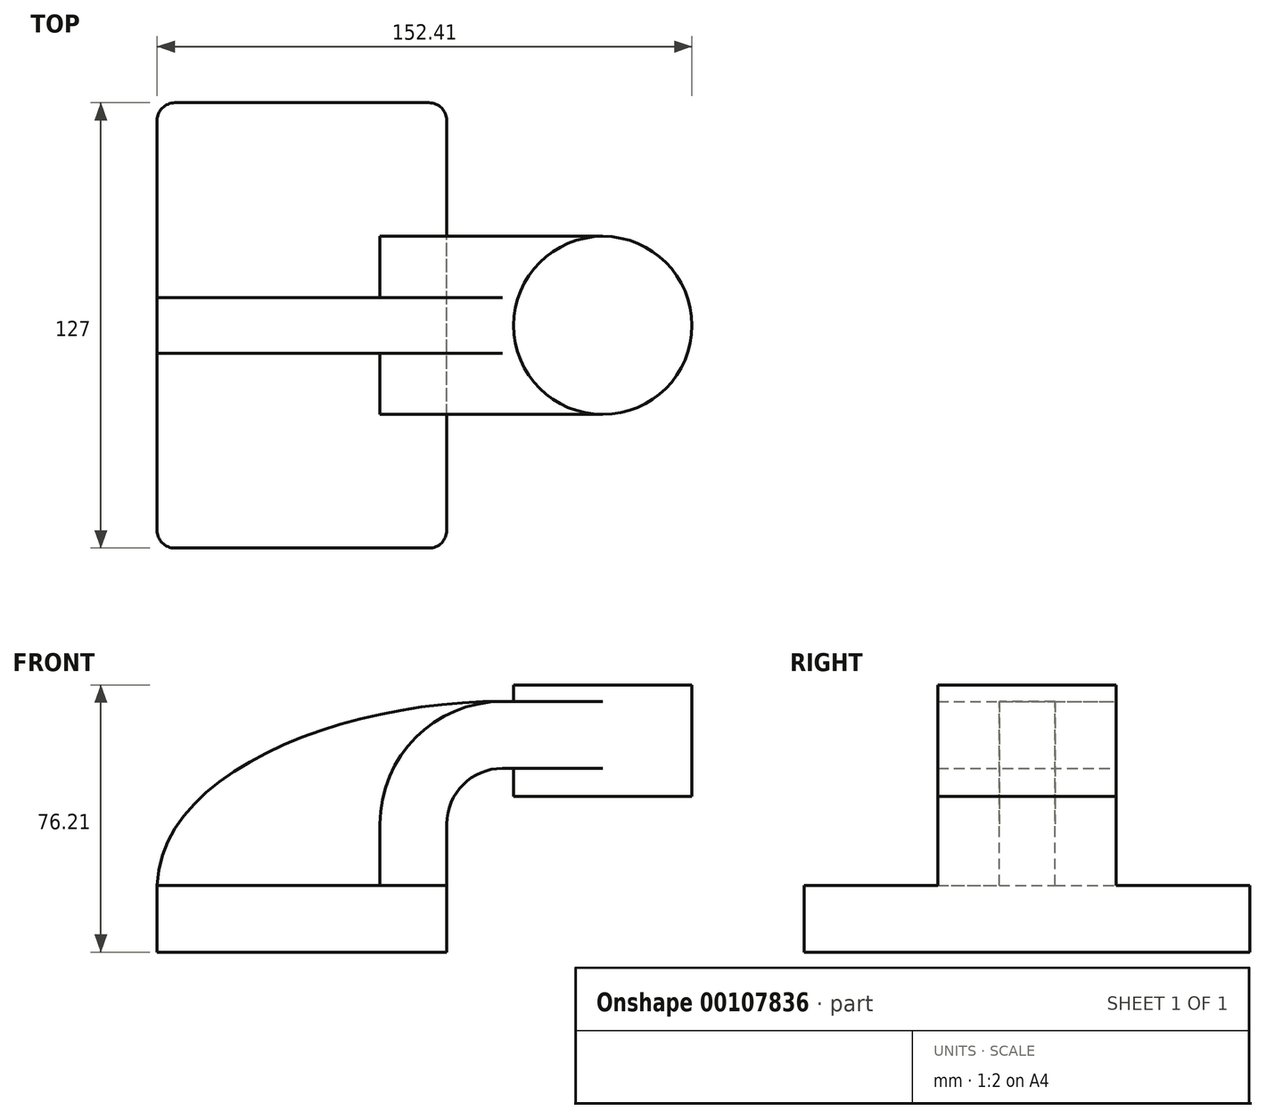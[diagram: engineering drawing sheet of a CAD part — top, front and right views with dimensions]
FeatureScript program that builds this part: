
annotation { "Feature Type Name" : "Feature", "Feature Type Description" : "" }
export const myFeature = defineFeature(function(context is Context, id is Id, definition is map)
    precondition{}
    {
        {
            var Q0;
            Q0=qCreatedBy(makeId("Front.planeOp"),FACE);
            var sketch = newSketch(context, id + "F0", { "sketchPlane" : qUnion([Q0])});
            skLineSegment(sketch, "E0.bottom", {"start": v(-41.27, -9.53) * mm, "end": v(41.28, -9.53) * mm});
            skLineSegment(sketch, "E0.top", {"start": v(-41.28, 9.53) * mm, "end": v(41.28, 9.53) * mm});
            skLineSegment(sketch, "E0.left", {"start": v(-41.28, -9.53) * mm, "end": v(-41.28, 9.53) * mm});
            skLineSegment(sketch, "E0.right", {"start": v(41.28, -9.53) * mm, "end": v(41.28, 9.53) * mm});
            skPoint(sketch, "E0.middle", {"position": v(0, 0) * mm});
            skLineSegment(sketch, "E1.bottom", {"start": v(111.12, 66.68) * mm, "end": v(60.32, 66.68) * mm});
            skLineSegment(sketch, "E1.top", {"start": v(111.12, 34.93) * mm, "end": v(60.33, 34.93) * mm});
            skLineSegment(sketch, "E1.left", {"start": v(111.12, 66.68) * mm, "end": v(111.12, 34.93) * mm});
            skLineSegment(sketch, "E1.right", {"start": v(60.32, 66.68) * mm, "end": v(60.33, 34.93) * mm});
            skPoint(sketch, "E1.middle", {"position": v(85.72, 50.8) * mm});
            skLineSegment(sketch, "E2", {"start": v(41.28, 9.53) * mm, "end": v(41.28, 27) * mm});
            skLineSegment(sketch, "E3", {"start": v(85.72, 42.88) * mm, "end": v(57.15, 42.88) * mm});
            skArc(sketch, "E4", {"start": v(57.15, 42.88) * mm, "mid": v(45.92, 38.23) * mm, "end": v(41.28, 27) * mm});
            skLineSegment(sketch, "E5.0", {"start": v(85.72, 61.93) * mm, "end": v(57.15, 61.93) * mm});
            skArc(sketch, "E5.1", {"start": v(57.15, 61.93) * mm, "mid": v(32.45, 51.7) * mm, "end": v(22.23, 27) * mm});
            skLineSegment(sketch, "E5.2", {"start": v(22.23, 9.53) * mm, "end": v(22.23, 27) * mm});
            skLineSegment(sketch, "E6", {"start": v(85.72, 66.68) * mm, "end": v(85.72, 34.93) * mm});
            skFitSpline(sketch, "E7", {"points": [v(-41.28, 9.53) * mm, v(57.15, 61.93) * mm], "startDerivative": vector(3.36, 100.4) * mm, "endDerivative": vector(128.86, -1.15) * mm});
            skSolve(sketch);
        }
        {
            var Q0;
            Q0=makeQuery(id+"F0.imprint","IMPRINT",FACE,{"disambiguationData":[TD([[makeQuery(id+"F0.imprint","IMPRINT",EDGE,{"derivedFrom":sQuery(id+"F0.wireOp",EDGE,"E0.bottom")}),1.0]])]});
            extrude(context, id + "F1", {"entities" : qUnion([Q0]), "endBound" : BoundingType.SYMMETRIC, "depth" : 127 * mm});
        }
        {
            var Q0;
            {var subQ4=sQuery(id+"F0.wireOp",EDGE,"E2");Q0=makeQuery(id+"F0.imprint","IMPRINT",FACE,{"disambiguationData":[TD([[makeQuery(id+"F0.imprint","IMPRINT",EDGE,{"derivedFrom":subQ4}),1.0]])]});}
            var Q1;
            {var subQ0=sQuery(id+"F0.wireOp",EDGE,"E5.0");var subQ1=sQuery(id+"F0.wireOp",EDGE,"E1.right");var subQ2=makeQuery(id+"F0.imprint","INTERSECT",VERTEX,{"derivedFrom":[subQ1,subQ0]});Q1=makeQuery(id+"F0.imprint","IMPRINT",FACE,{"disambiguationData":[TD([[makeQuery(id+"F0.imprint","IMPRINT",EDGE,{"disambiguationData":[TD([[subQ2,-1.0]])],"derivedFrom":subQ1}),1.0]])]});}
            extrude(context, id + "F2", {"entities" : qUnion([Q0, Q1]), "operationType" : NewBodyOperationType.ADD, "endBound" : BoundingType.SYMMETRIC, "depth" : 50.8 * mm});
        }
        {
            var Q0;
            Q0=makeQuery(id+"F0.imprint","IMPRINT",FACE,{"disambiguationData":[TD([[makeQuery(id+"F0.imprint","IMPRINT",EDGE,{"derivedFrom":sQuery(id+"F0.wireOp",EDGE,"E5.1")}),-1.0]])]});
            extrude(context, id + "F3", {"entities" : qUnion([Q0]), "operationType" : NewBodyOperationType.ADD, "endBound" : BoundingType.SYMMETRIC, "depth" : 15.88 * mm});
        }
        {
            var Q0;
            {var subQ0=sQuery(id+"F0.wireOp",EDGE,"E1.left");Q0=makeQuery(id+"F0.imprint","IMPRINT",FACE,{"disambiguationData":[TD([[makeQuery(id+"F0.imprint","IMPRINT",EDGE,{"derivedFrom":subQ0}),-1.0]])]});}
            var Q1;
            Q1=sQuery(id+"F0.wireOp",EDGE,"E6");
            revolve(context, id + "F4", {"operationType" : NewBodyOperationType.ADD, "entities" : qUnion([Q0]), "axis" : qUnion([Q1]), "revolveType" : RevolveType.FULL});
        }
        {
            var Q0;
            Q0=makeQuery(id+"F1.opExtrude","CAP_EDGE",EDGE,{"disambiguationData":[OSD([sQuery(id+"F0.wireOp",EDGE,"E0.right")])],"isStart":false});
            var Q1;
            Q1=makeQuery(id+"F1.opExtrude","CAP_EDGE",EDGE,{"disambiguationData":[OSD([sQuery(id+"F0.wireOp",EDGE,"E0.left")])],"isStart":false});
            var Q2;
            Q2=makeQuery(id+"F1.opExtrude","CAP_EDGE",EDGE,{"disambiguationData":[OSD([sQuery(id+"F0.wireOp",EDGE,"E0.left")])],"isStart":true});
            var Q3;
            Q3=makeQuery(id+"F1.opExtrude","CAP_EDGE",EDGE,{"disambiguationData":[OSD([sQuery(id+"F0.wireOp",EDGE,"E0.right")])],"isStart":true});
            fillet(context, id + "F5", {"entities" : qUnion([Q0, Q1, Q2, Q3]), "radius" : 5.08 * mm, "tangentPropagation" : true, "allowEdgeOverflow" : false});
        }
    });
